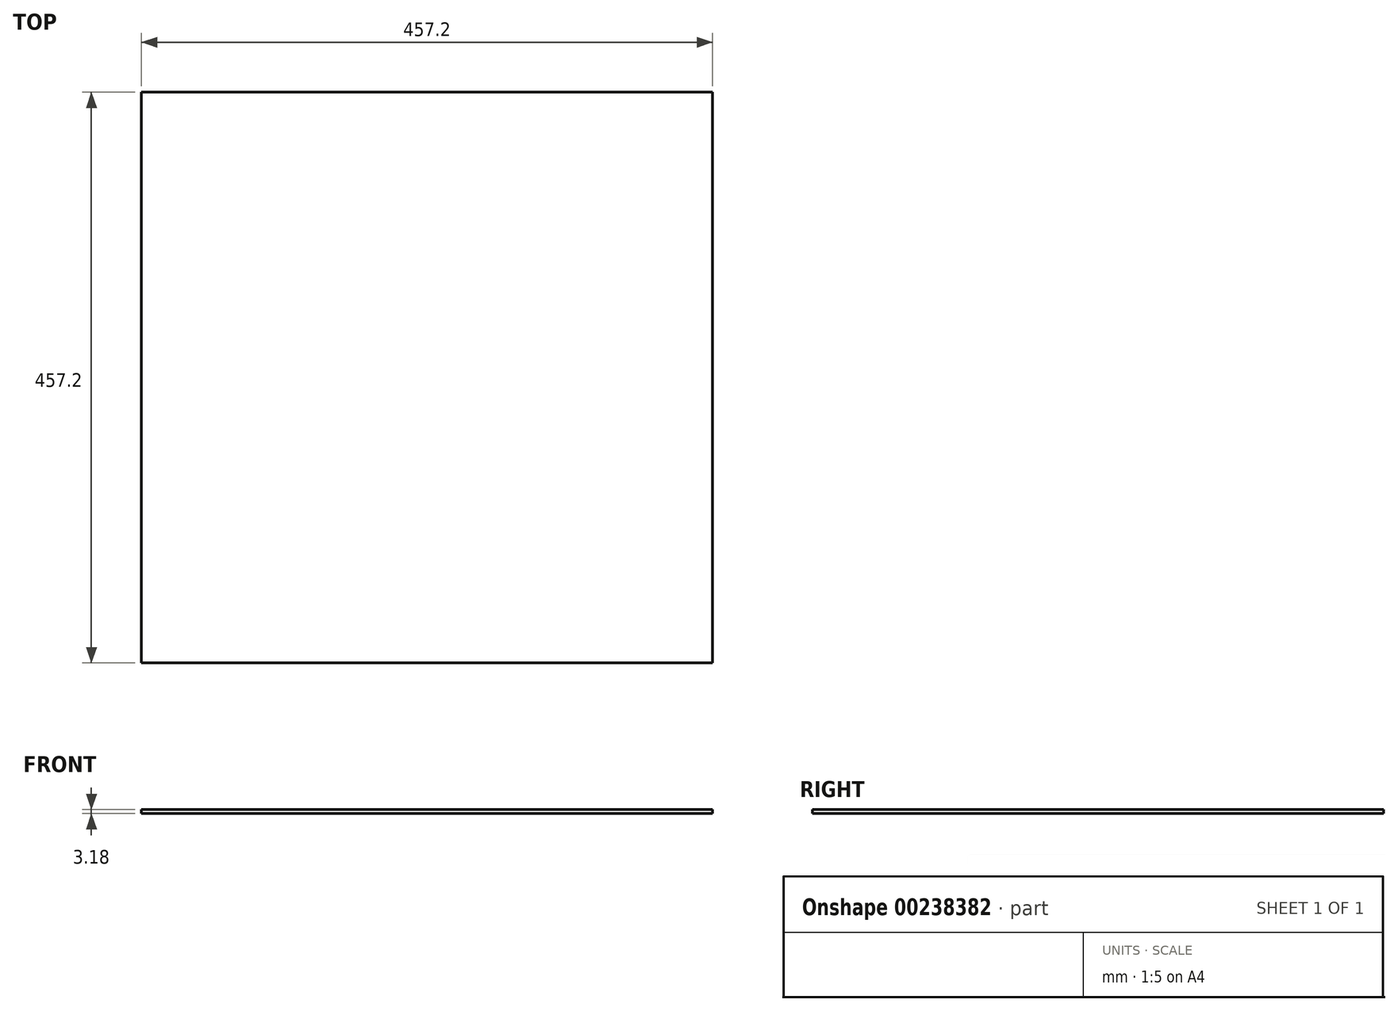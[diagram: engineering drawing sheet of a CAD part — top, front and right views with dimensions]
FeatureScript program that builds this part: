
annotation { "Feature Type Name" : "Feature", "Feature Type Description" : "" }
export const myFeature = defineFeature(function(context is Context, id is Id, definition is map)
    precondition{}
    {
        {
            var Q0;
            Q0=qCreatedBy(makeId("Top.planeOp"),FACE);
            var sketch = newSketch(context, id + "F0", { "sketchPlane" : qUnion([Q0])});
            skLineSegment(sketch, "E0.bottom", {"start": v(228.6, 228.6) * mm, "end": v(-228.6, 228.6) * mm});
            skLineSegment(sketch, "E0.top", {"start": v(228.6, -228.6) * mm, "end": v(-228.6, -228.6) * mm});
            skLineSegment(sketch, "E0.left", {"start": v(228.6, 228.6) * mm, "end": v(228.6, -228.6) * mm});
            skLineSegment(sketch, "E0.right", {"start": v(-228.6, 228.6) * mm, "end": v(-228.6, -228.6) * mm});
            skPoint(sketch, "E0.middle", {"position": v(0, 0) * mm});
            skSolve(sketch);
        }
        {
            var Q0;
            Q0 = qSketchRegion(id + "F0", true);
            extrude(context, id + "F1", {"entities" : qUnion([Q0]), "endBound" : BoundingType.SYMMETRIC, "depth" : 3.17 * mm});
        }
    });
